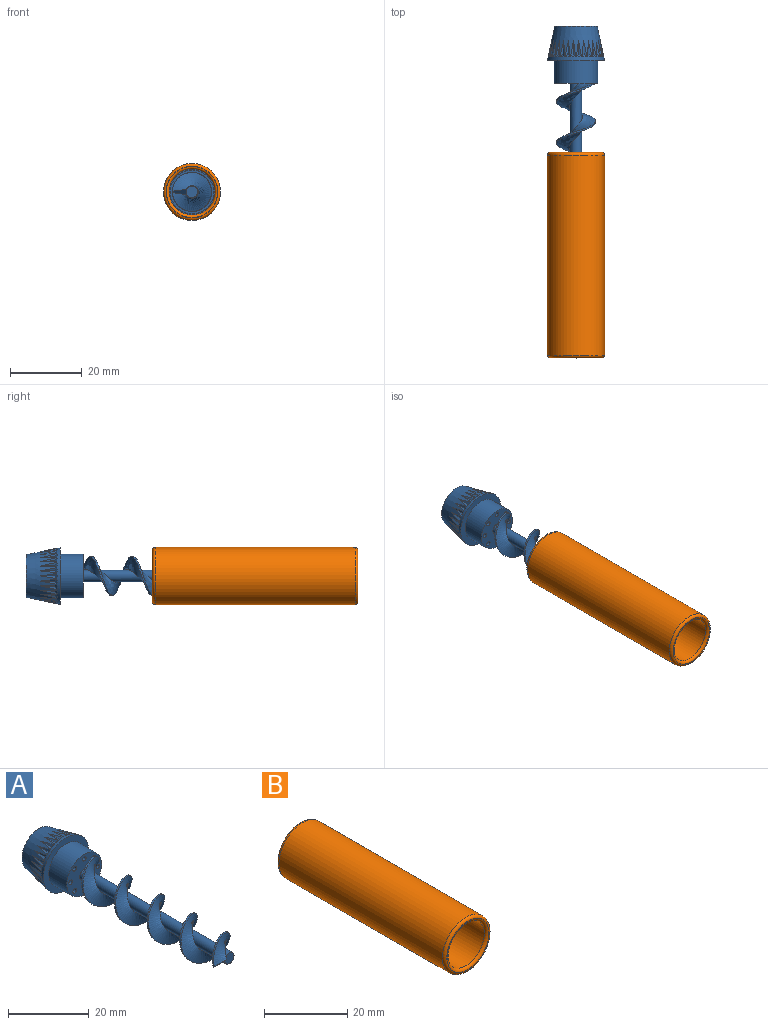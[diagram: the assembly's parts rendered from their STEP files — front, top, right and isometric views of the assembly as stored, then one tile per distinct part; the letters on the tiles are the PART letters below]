
ASSEMBLY  parts=2 mates=1
PART A: 111 faces, bbox 16x67.4x16 mm
  f0: cylinder r=0.64mm len=15.88mm, axis (0,-1,0), area 63.3mm2, adj f101,f104
  f1: cylinder r=0.64mm len=15.88mm, axis (0,-1,0), area 63.3mm2, adj f12,f101,f104
  f2: cylinder r=0.64mm len=15.88mm, axis (0,-1,0), area 63.3mm2, adj f101,f104
  f3: cylinder r=0.64mm len=15.88mm, axis (0,-1,0), area 63.3mm2, adj f101,f104
  f4: cylinder r=0.64mm len=15.88mm, axis (0,-1,0), area 63.3mm2, adj f101,f104
  f5: cylinder r=0.64mm len=15.88mm, axis (0,-1,0), area 63.3mm2, adj f101,f104
  f6: cylinder r=0.64mm len=15.88mm, axis (0,-1,0), area 63.3mm2, adj f101,f104
  f7: plane 3.83x1.49mm, normal (0,-0.75,-0.66), area 4.8mm2, adj f8,f9,f10,f11,f12,f108,f109
  f8: bspline ~52.74x3.79mm, area 41.9mm2, adj f7,f10,f104,f109
  f9: bspline ~54.17x3.79mm, area 42.7mm2, adj f7,f12,f104,f108,f109
  f10: bspline ~51.12x10.8mm, area 427.5mm2, adj f7,f8,f11,f104
  f11: bspline ~51.3x10.79mm, area 70mm2, adj f7,f10,f12,f104
  f12: bspline ~53.35x11mm, area 433.7mm2, adj f1,f7,f9,f11,f104
  f13: plane 1.49x0.7mm, normal (-0.73,0.67,0.15), area 0.6mm2, adj f14,f15,f100
  f14: plane 4.64x1.14mm, normal (-0.74,0.1,0.66), area 1.7mm2, adj f13,f15,f100
  f15: plane 4.64x0.96mm, normal (-0.95,0.1,-0.3), area 1.7mm2, adj f13,f14,f100
  f16: plane 1.4x0.81mm, normal (-0.68,0.67,0.3), area 0.6mm2, adj f17,f18,f100
  f17: plane 4.64x1.22mm, normal (-0.59,0.1,0.8), area 1.7mm2, adj f16,f18,f100
  f18: plane 4.64x1.1mm, normal (-0.99,0.1,-0.1), area 1.7mm2, adj f16,f17,f100
  f19: plane 1.25x0.93mm, normal (-0.6,0.67,0.44), area 0.6mm2, adj f20,f21,f100
  f20: plane 4.64x1.25mm, normal (-0.41,0.1,0.91), area 1.7mm2, adj f19,f21,f100
  f21: plane 4.64x1.2mm, normal (-0.99,0.1,0.11), area 1.7mm2, adj f19,f20,f100
  f22: plane 1.16x1.05mm, normal (-0.5,0.67,0.55), area 0.6mm2, adj f23,f24,f100
  f23: plane 4.64x1.23mm, normal (-0.21,0.1,0.97), area 1.7mm2, adj f22,f24,f100
  f24: plane 4.64x1.24mm, normal (-0.94,0.1,0.31), area 1.7mm2, adj f22,f23,f100
  f25: plane 1.33x0.86mm, normal (-0.37,0.67,0.64), area 0.6mm2, adj f26,f27,f100
  f26: plane 4.64x1.16mm, normal (0,0.1,0.99), area 1.7mm2, adj f25,f27,f100
  f27: plane 4.64x1.24mm, normal (-0.86,0.1,0.5), area 1.7mm2, adj f25,f26,f100
  f28: plane 1.45x0.76mm, normal (-0.23,0.67,0.71), area 0.6mm2, adj f29,f30,f100
  f29: plane 4.64x1.04mm, normal (0.2,0.1,0.97), area 1.7mm2, adj f28,f30,f100
  f30: plane 4.64x1.18mm, normal (-0.74,0.1,0.67), area 1.7mm2, adj f28,f29,f100
  f31: plane 1.51x0.66mm, normal (-0.08,0.67,0.74), area 0.6mm2, adj f32,f33,f100
  f32: plane 4.64x0.93mm, normal (0.4,0.1,0.91), area 1.7mm2, adj f31,f33,f100
  f33: plane 4.64x1.08mm, normal (-0.58,0.1,0.81), area 1.7mm2, adj f31,f32,f100
  f34: plane 1.51x0.66mm, normal (0.08,0.67,0.74), area 0.6mm2, adj f35,f36,f100
  f35: plane 4.64x1.08mm, normal (0.58,0.1,0.81), area 1.7mm2, adj f34,f36,f100
  f36: plane 4.64x0.93mm, normal (-0.4,0.1,0.91), area 1.7mm2, adj f34,f35,f100
  f37: plane 1.45x0.76mm, normal (0.23,0.67,0.71), area 0.6mm2, adj f38,f39,f100
  f38: plane 4.64x1.18mm, normal (0.74,0.1,0.67), area 1.7mm2, adj f37,f39,f100
  f39: plane 4.64x1.04mm, normal (-0.2,0.1,0.97), area 1.7mm2, adj f37,f38,f100
  f40: plane 1.33x0.86mm, normal (0.37,0.67,0.64), area 0.6mm2, adj f41,f42,f100
  f41: plane 4.64x1.24mm, normal (0.86,0.1,0.5), area 1.7mm2, adj f40,f42,f100
  f42: plane 4.64x1.16mm, normal (0,0.1,0.99), area 1.7mm2, adj f40,f41,f100
  f43: plane 1.16x1.05mm, normal (0.5,0.67,0.55), area 0.6mm2, adj f44,f45,f100
  f44: plane 4.64x1.24mm, normal (0.94,0.1,0.31), area 1.7mm2, adj f43,f45,f100
  f45: plane 4.64x1.23mm, normal (0.21,0.1,0.97), area 1.7mm2, adj f43,f44,f100
  f46: plane 1.25x0.93mm, normal (0.6,0.67,0.44), area 0.6mm2, adj f47,f48,f100
  f47: plane 4.64x1.2mm, normal (0.99,0.1,0.11), area 1.7mm2, adj f46,f48,f100
  f48: plane 4.64x1.25mm, normal (0.41,0.1,0.91), area 1.7mm2, adj f46,f47,f100
  f49: plane 1.4x0.81mm, normal (0.68,0.67,0.3), area 0.6mm2, adj f50,f51,f100
  f50: plane 4.64x1.1mm, normal (0.99,0.1,-0.1), area 1.7mm2, adj f49,f51,f100
  f51: plane 4.64x1.22mm, normal (0.59,0.1,0.8), area 1.7mm2, adj f49,f50,f100
  f52: plane 1.49x0.7mm, normal (0.73,0.67,0.15), area 0.6mm2, adj f53,f54,f100
  f53: plane 4.64x0.96mm, normal (0.95,0.1,-0.3), area 1.7mm2, adj f52,f54,f100
  f54: plane 4.64x1.14mm, normal (0.74,0.1,0.66), area 1.7mm2, adj f52,f53,f100
  f55: plane 1.52x0.66mm, normal (0.74,0.67,0), area 0.6mm2, adj f56,f57,f100
  f56: plane 4.64x1.01mm, normal (0.86,0.1,-0.49), area 1.7mm2, adj f55,f57,f100
  f57: plane 4.64x1.01mm, normal (0.86,0.1,0.49), area 1.7mm2, adj f55,f56,f100
  f58: plane 1.49x0.7mm, normal (0.73,0.67,-0.15), area 0.6mm2, adj f59,f60,f100
  f59: plane 4.64x1.14mm, normal (0.74,0.1,-0.66), area 1.7mm2, adj f58,f60,f100
  f60: plane 4.64x0.96mm, normal (0.95,0.1,0.3), area 1.7mm2, adj f58,f59,f100
  f61: plane 1.4x0.81mm, normal (0.68,0.67,-0.3), area 0.6mm2, adj f62,f63,f100
  f62: plane 4.64x1.22mm, normal (0.59,0.1,-0.8), area 1.7mm2, adj f61,f63,f100
  f63: plane 4.64x1.1mm, normal (0.99,0.1,0.1), area 1.7mm2, adj f61,f62,f100
  f64: plane 1.25x0.93mm, normal (0.6,0.67,-0.44), area 0.6mm2, adj f65,f66,f100
  f65: plane 4.64x1.25mm, normal (0.41,0.1,-0.91), area 1.7mm2, adj f64,f66,f100
  f66: plane 4.64x1.2mm, normal (0.99,0.1,-0.11), area 1.7mm2, adj f64,f65,f100
  f67: plane 1.16x1.05mm, normal (0.5,0.67,-0.55), area 0.6mm2, adj f68,f69,f100
  f68: plane 4.64x1.23mm, normal (0.21,0.1,-0.97), area 1.7mm2, adj f67,f69,f100
  f69: plane 4.64x1.24mm, normal (0.94,0.1,-0.31), area 1.7mm2, adj f67,f68,f100
  f70: plane 1.33x0.86mm, normal (0.37,0.67,-0.64), area 0.6mm2, adj f71,f72,f100
  f71: plane 4.64x1.16mm, normal (0,0.1,-0.99), area 1.7mm2, adj f70,f72,f100
  f72: plane 4.64x1.24mm, normal (0.86,0.1,-0.5), area 1.7mm2, adj f70,f71,f100
  f73: plane 1.45x0.76mm, normal (0.23,0.67,-0.71), area 0.6mm2, adj f74,f75,f100
  f74: plane 4.64x1.04mm, normal (-0.2,0.1,-0.97), area 1.7mm2, adj f73,f75,f100
  f75: plane 4.64x1.18mm, normal (0.74,0.1,-0.67), area 1.7mm2, adj f73,f74,f100
  f76: plane 1.51x0.66mm, normal (0.08,0.67,-0.74), area 0.6mm2, adj f77,f78,f100
  f77: plane 4.64x0.93mm, normal (-0.4,0.1,-0.91), area 1.7mm2, adj f76,f78,f100
  f78: plane 4.64x1.08mm, normal (0.58,0.1,-0.81), area 1.7mm2, adj f76,f77,f100
  f79: plane 1.51x0.66mm, normal (-0.08,0.67,-0.74), area 0.6mm2, adj f80,f81,f100
  f80: plane 4.64x1.08mm, normal (-0.58,0.1,-0.81), area 1.7mm2, adj f79,f81,f100
  f81: plane 4.64x0.93mm, normal (0.4,0.1,-0.91), area 1.7mm2, adj f79,f80,f100
  f82: plane 1.45x0.76mm, normal (-0.23,0.67,-0.71), area 0.6mm2, adj f83,f84,f100
  f83: plane 4.64x1.18mm, normal (-0.74,0.1,-0.67), area 1.7mm2, adj f82,f84,f100
  f84: plane 4.64x1.04mm, normal (0.2,0.1,-0.97), area 1.7mm2, adj f82,f83,f100
  f85: plane 1.33x0.86mm, normal (-0.37,0.67,-0.64), area 0.6mm2, adj f86,f87,f100
  f86: plane 4.64x1.24mm, normal (-0.86,0.1,-0.5), area 1.7mm2, adj f85,f87,f100
  f87: plane 4.64x1.16mm, normal (0,0.1,-0.99), area 1.7mm2, adj f85,f86,f100
  f88: plane 1.16x1.05mm, normal (-0.5,0.67,-0.55), area 0.6mm2, adj f89,f90,f100
  f89: plane 4.64x1.24mm, normal (-0.94,0.1,-0.31), area 1.7mm2, adj f88,f90,f100
  f90: plane 4.64x1.23mm, normal (-0.21,0.1,-0.97), area 1.7mm2, adj f88,f89,f100
  f91: plane 1.25x0.93mm, normal (-0.6,0.67,-0.44), area 0.6mm2, adj f92,f93,f100
  f92: plane 4.64x1.2mm, normal (-0.99,0.1,-0.11), area 1.7mm2, adj f91,f93,f100
  f93: plane 4.64x1.25mm, normal (-0.41,0.1,-0.91), area 1.7mm2, adj f91,f92,f100
  f94: plane 1.4x0.81mm, normal (-0.68,0.67,-0.3), area 0.6mm2, adj f95,f96,f100
  f95: plane 4.64x1.1mm, normal (-0.99,0.1,0.1), area 1.7mm2, adj f94,f96,f100
  f96: plane 4.64x1.22mm, normal (-0.59,0.1,-0.8), area 1.7mm2, adj f94,f95,f100
  f97: plane 1.49x0.7mm, normal (-0.73,0.67,-0.15), area 0.6mm2, adj f98,f99,f100
  f98: plane 4.64x0.96mm, normal (-0.95,0.1,0.3), area 1.7mm2, adj f97,f99,f100
  f99: plane 4.64x1.14mm, normal (-0.74,0.1,-0.66), area 1.7mm2, adj f97,f98,f100
  f100: cone r=7.94mm half-angle=12deg, axis (0,-1,0), area 327.9mm2, adj f13,f14,f15,f16,f17,f18,f19,f20
  f101: plane 11.83x11.83mm, normal (0,1,0), area 99.7mm2, adj f0,f1,f2,f3,f4,f5,f6,f100
  f102: plane 15.88x15.88mm, normal (0,-1,0), area 81.2mm2, adj f100,f103
  f103: cylinder r=6.1mm len=12.19mm, axis (0,1,0), area 243.2mm2, adj f102,f104
  f104: plane 12.25x12.25mm, normal (0,-1,0), area 89.6mm2, adj f0,f1,f2,f3,f4,f5,f6,f8
  f105: plane 1.52x0.66mm, normal (-0.74,0.67,0), area 0.6mm2, adj f100,f106,f107
  f106: plane 4.64x1.01mm, normal (-0.86,0.1,0.49), area 1.7mm2, adj f100,f105,f107
  f107: plane 4.64x1.01mm, normal (-0.86,0.1,-0.49), area 1.7mm2, adj f100,f105,f106
  f108: plane 3.23x3.23mm, normal (0,-1,0), area 8.2mm2, adj f7,f9,f109
  f109: cylinder r=1.61mm len=50.8mm, axis (0,1,0), area 461.2mm2, adj f7,f8,f9,f104,f108
  f110: cylinder r=0.64mm len=15.88mm, axis (0,-1,0), area 63.3mm2, adj f101,f104
PART B: 8 faces, bbox 17.2x57.2x17.2 mm
  f0: cylinder r=7.94mm len=55.63mm, axis (0,1,0), area 2774.2mm2, adj f6,f7
  f1: plane 14.35x14.35mm, normal (0,-1,0), area 2.9mm2, adj f5,f7
  f2: plane 14.35x14.35mm, normal (0,1,0), area 2.9mm2, adj f4,f6
  f3: cylinder r=6.35mm len=55.63mm, axis (0,1,0), area 2219.4mm2, adj f4,f5
  f4: torus R=7.11mm, axis (0,-1,0), area 49.8mm2, adj f2,f3
  f5: torus R=7.11mm, axis (0,-1,0), area 49.8mm2, adj f1,f3
  f6: torus R=7.18mm, axis (0,-1,0), area 57.6mm2, adj f0,f2
  f7: torus R=7.18mm, axis (0,-1,0), area 57.6mm2, adj f0,f1
PLACE A t=(2.16,-67.54,-6.57)mm fixed
PLACE B t=(2.16,-93.14,-6.57)mm
MATE slider A.f103 <-> B.f0  axis (0,-1,0) through (2.16,-67.54,-6.57)mm
